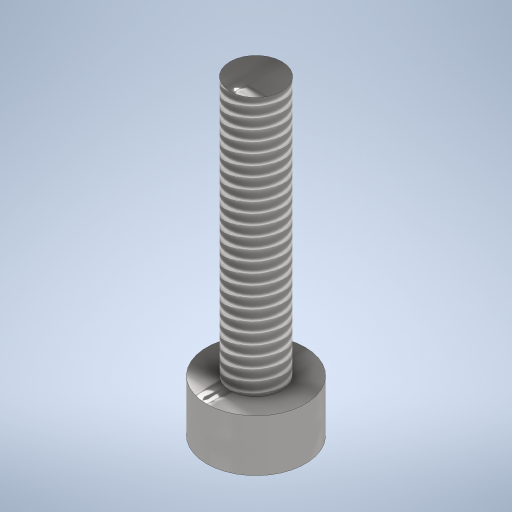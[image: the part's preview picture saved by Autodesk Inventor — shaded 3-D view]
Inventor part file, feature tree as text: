
AUTODESK INVENTOR PART (.ipt)
format: ipt  version: 2024.2 (Build 282272000, 272)  size: 311,296 bytes
history: native  units: mm
features: sketch x2, revolve x1, thread x1, extrude x1
ambient origin geometry x8: Origin, YZ Plane, XZ Plane, XY Plane, X Axis, Y Axis, Z Axis, Center Point
bodies: Solid1 (feature_tree)
feature tree (5):
  revolve  "Revolution1"  [1 undecoded]
  thread  "Thread1"  [1 undecoded]
  extrude  "Extrusion1"  [1 undecoded]
  sketch  "Sketch1"  dims[d4=90.0deg d5=10.0mm d6=0.0mm d0=0.0mm]
  sketch  "Sketch2"
note: 3 required parameter values undecoded (feature->parameter linkage not recoverable at this tier; creation-order binding heuristic only, values carry confidence <= 0.55)